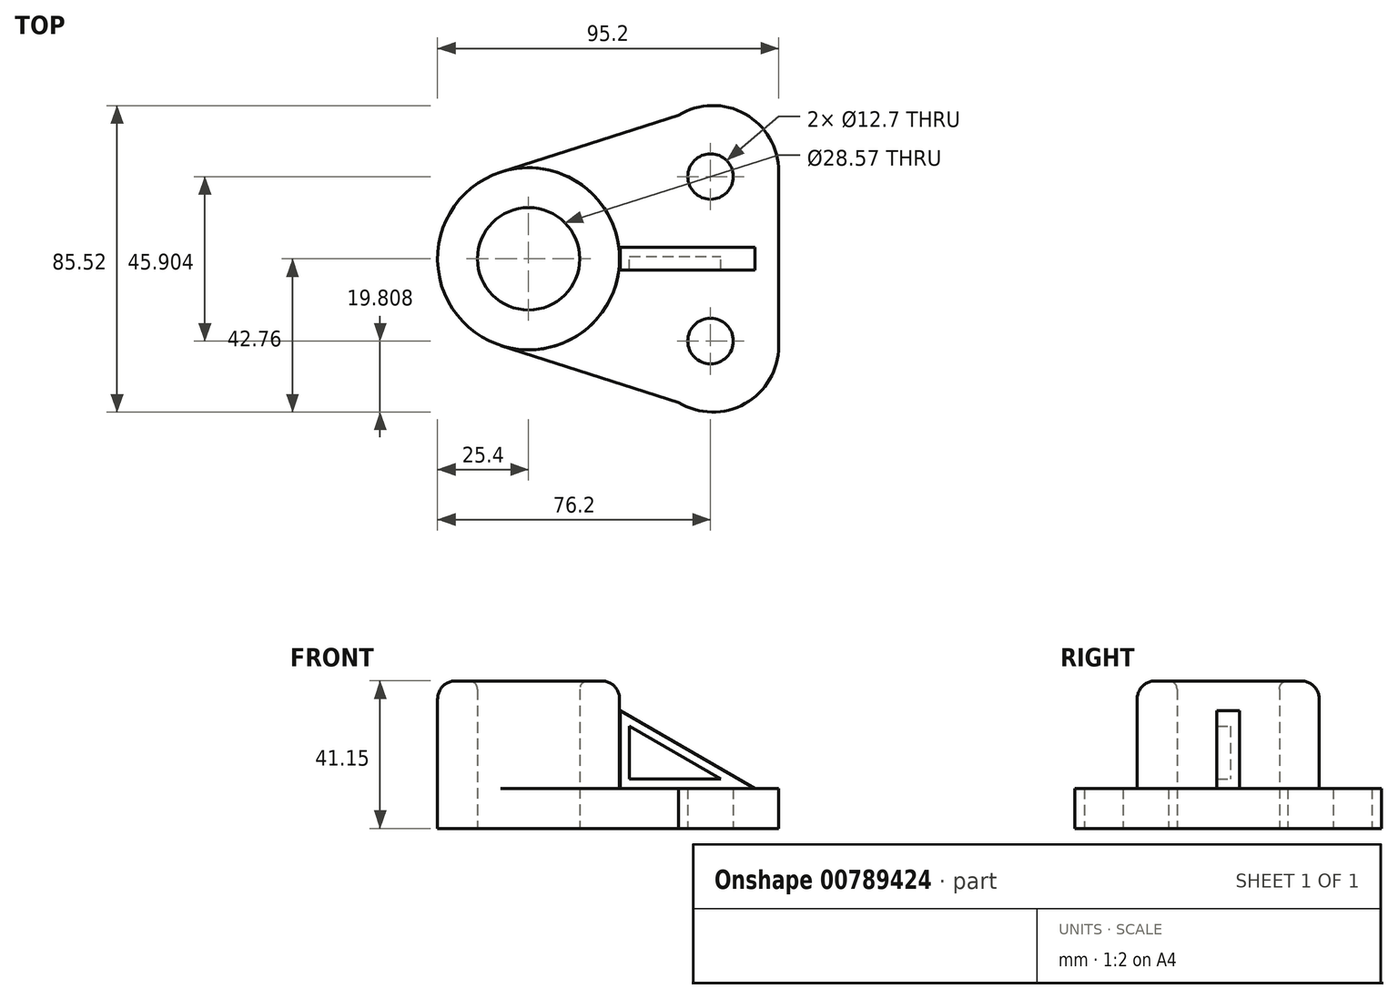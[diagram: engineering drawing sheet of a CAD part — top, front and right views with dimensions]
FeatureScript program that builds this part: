
annotation { "Feature Type Name" : "Feature", "Feature Type Description" : "" }
export const myFeature = defineFeature(function(context is Context, id is Id, definition is map)
    precondition{}
    {
        {
            var Q0;
            Q0=qCreatedBy(makeId("Top.planeOp"),FACE);
            var sketch = newSketch(context, id + "F0", { "sketchPlane" : qUnion([Q0])});
            skLineSegment(sketch, "E0", {"start": v(0, -3.9) * mm, "end": v(0, -22.95) * mm, "construction": true});
            skArc(sketch, "E1", {"start": v(19, -24.37) * mm, "mid": v(19.05, -22.95) * mm, "end": v(19, -21.54) * mm});
            skCircle(sketch, "E2", {"center": v(0, -22.95) * mm, "radius": 6.35 * mm});
            skLineSegment(sketch, "E3", {"start": v(0, -22.95) * mm, "end": v(-6.35, -22.95) * mm, "construction": true});
            skLineSegment(sketch, "E4", {"start": v(-50.8, -22.95) * mm, "end": v(-50.8, 0) * mm, "construction": true});
            skCircle(sketch, "E5", {"center": v(-50.8, 0) * mm, "radius": 25.4 * mm});
            skCircle(sketch, "E6", {"center": v(-50.8, 0) * mm, "radius": 14.29 * mm});
            skLineSegment(sketch, "E7", {"start": v(-58.55, -24.19) * mm, "end": v(-8.94, -40.1) * mm});
            skPoint(sketch, "E8.end.orphan", {"position": v(-8.94, 51.02) * mm});
            skPoint(sketch, "E8.start.orphan", {"position": v(-58.55, 24.19) * mm});
            skPoint(sketch, "E9.orphan", {"position": v(0, 34.2) * mm});
            skLineSegment(sketch, "E10", {"start": v(19, -24.37) * mm, "end": v(19, 0) * mm});
            skLineSegment(sketch, "E11", {"start": v(19, 0) * mm, "end": v(-25.4, 0) * mm});
            skArc(sketch, "E12", {"start": v(-8.94, -40.1) * mm, "mid": v(9.62, -40.4) * mm, "end": v(19, -24.37) * mm});
            skSolve(sketch);
        }
        {
            var Q0;
            Q0=makeQuery(id+"F0.imprint","IMPRINT",FACE,{"disambiguationData":[TD([[makeQuery(id+"F0.imprint","IMPRINT",EDGE,{"derivedFrom":sQuery(id+"F0.wireOp",EDGE,"E6")}),-1.0]])]});
            extrude(context, id + "F1", {"entities" : qUnion([Q0]), "depth" : 41.15 * mm, "offsetDistance" : 25.4 * mm});
        }
        {
            var Q0;
            Q0=makeQuery(id+"F0.imprint","IMPRINT",FACE,{"disambiguationData":[TD([[makeQuery(id+"F0.imprint","IMPRINT",EDGE,{"derivedFrom":sQuery(id+"F0.wireOp",EDGE,"E2")}),-1.0]])]});
            extrude(context, id + "F2", {"entities" : qUnion([Q0]), "operationType" : NewBodyOperationType.ADD, "depth" : 11.18 * mm, "offsetDistance" : 25.4 * mm});
        }
        {
            var Q0;
            Q0=makeQuery(id+"F2.opExtrude","CAP_FACE",FACE,{"disambiguationData":[OSD([sQuery(id+"F0.wireOp",EDGE,"E2"),sQuery(id+"F0.wireOp",EDGE,"E5"),sQuery(id+"F0.wireOp",EDGE,"E7"),sQuery(id+"F0.wireOp",EDGE,"E10"),sQuery(id+"F0.wireOp",EDGE,"E11"),sQuery(id+"F0.wireOp",EDGE,"E12")])],"isStart":false});
            var sketch = newSketch(context, id + "F3", { "sketchPlane" : qUnion([Q0])});
            skPoint(sketch, "E13.0", {"position": v(-25.4, 0) * mm});
            skLineSegment(sketch, "E14.0", {"start": v(19, 0) * mm, "end": v(-25.4, 0) * mm});
            skCircle(sketch, "E15.0", {"center": v(-50.8, 0) * mm, "radius": 25.4 * mm});
            skLineSegment(sketch, "E16", {"start": v(19, 0) * mm, "end": v(15.7, 0) * mm, "construction": true});
            skLineSegment(sketch, "E17", {"start": v(15.7, 0) * mm, "end": v(-25.4, 0) * mm});
            skLineSegment(sketch, "E18", {"start": v(-25.4, 0) * mm, "end": v(15.7, 0) * mm});
            skSolve(sketch);
        }
        {
            var Q0;
            Q0=qSketchRegion(id+"F3",true);
            extrude(context, id + "F4", {"entities" : qUnion([Q0]), "operationType" : NewBodyOperationType.ADD, "depth" : 25.4 * mm, "offsetDistance" : 25.4 * mm});
        }
        {
            var sketch = newSketch(context, id + "F5", { "sketchPlane" : qUnion([])});
            skLineSegment(sketch, "E19", {"start": v(0, 41.4) * mm, "end": v(0, 11.3) * mm});
            skSolve(sketch);
        }
        {
            var Q0;
            Q0=makeQuery(id+"F3.imprint","IMPRINT",FACE,{"disambiguationData":[TD([[makeQuery(id+"F3.imprint","IMPRINT",EDGE,{"derivedFrom":sQuery(id+"F3.wireOp",EDGE,"E14.0")}),1.0]])]});
            var sketch = newSketch(context, id + "F6", { "sketchPlane" : qUnion([Q0])});
            skLineSegment(sketch, "E20", {"start": v(-25.41, 0) * mm, "end": v(15.71, 0) * mm});
            skSolve(sketch);
        }
        {
            var Q0;
            Q0=makeQuery(id+"F1.opExtrude","SWEPT_BODY",BODY,{"disambiguationData":[OSD([sQuery(id+"F0.wireOp",EDGE,"E5"),sQuery(id+"F0.wireOp",EDGE,"E6")])]});
            var Q1;
            Q1=qCreatedBy(makeId("Front.planeOp"),FACE);
            mirror(context, id + "F7", {"operationType" : NewBodyOperationType.ADD, "entities" : qUnion([Q0]), "mirrorPlane" : qUnion([Q1])});
        }
        {
            var Q0;
            Q0=makeQuery(id+"F4.opExtrude","CAP_FACE",FACE,{"disambiguationData":[OSD([sQuery(id+"F3.wireOp",EDGE,"E15.0")])],"isStart":false});
            extrude(context, id + "F8", {"entities" : qUnion([Q0]), "operationType" : NewBodyOperationType.REMOVE, "endBound" : BoundingType.THROUGH_ALL, "oppositeDirection" : true, "depth" : 25.4 * mm, "offsetDistance" : 25.4 * mm});
        }
        {
            var Q0;
            Q0=qCreatedBy(makeId("Front.planeOp"),FACE);
            var sketch = newSketch(context, id + "F9", { "sketchPlane" : qUnion([Q0])});
            skLineSegment(sketch, "E21.0", {"start": v(-25.15, 41.4) * mm, "end": v(-25.15, 11.3) * mm});
            skLineSegment(sketch, "E22.0", {"start": v(-25.41, 11.18) * mm, "end": v(15.71, 11.18) * mm});
            skLineSegment(sketch, "E23", {"start": v(-25.15, 32.86) * mm, "end": v(12.41, 11.18) * mm});
            skLineSegment(sketch, "E24", {"start": v(-25.15, 32.86) * mm, "end": v(-25.15, 11.3) * mm});
            skLineSegment(sketch, "E25", {"start": v(12.41, 11.18) * mm, "end": v(-25.15, 11.3) * mm});
            skSolve(sketch);
        }
        {
            var Q0;
            Q0=makeQuery(id+"F1.opExtrude","CAP_EDGE",EDGE,{"disambiguationData":[OSD([sQuery(id+"F0.wireOp",EDGE,"E5")])],"isStart":false});
            var Q1;
            {var subQ0=makeQuery(id+"F2.opExtrude","CAP_EDGE",EDGE,{"disambiguationData":[OSD([sQuery(id+"F0.wireOp",EDGE,"E5")])],"isStart":false});Q1=makeQuery(id+"F7.boolean.opBoolean","MERGE",EDGE,{"derivedFrom":[subQ0,makeQuery(id+"F7.opPattern","COPY",EDGE,{"derivedFrom":subQ0,"instanceName":"1"})]});}
            fillet(context, id + "F10", {"entities" : qUnion([Q0, Q1]), "radius" : 5.08 * mm, "tangentPropagation" : true, "allowEdgeOverflow" : false});
        }
        {
            var Q0;
            {var subQ0=sQuery(id+"F9.wireOp",EDGE,"E23");Q0=makeQuery(id+"F9.imprint","IMPRINT",FACE,{"disambiguationData":[TD([[makeQuery(id+"F9.imprint","IMPRINT",EDGE,{"derivedFrom":subQ0}),-1.0]])]});}
            extrude(context, id + "F11", {"entities" : qUnion([Q0]), "depth" : 3.17 * mm, "offsetDistance" : 25.4 * mm, "hasSecondDirection" : true, "secondDirectionOppositeDirection" : true, "secondDirectionDepth" : 3.17 * mm});
        }
        {
            var Q0;
            Q0=makeQuery(id+"F11.opExtrude","CAP_FACE",FACE,{"disambiguationData":[OSD([sQuery(id+"F9.wireOp",EDGE,"E21.0"),sQuery(id+"F9.wireOp",EDGE,"E23"),sQuery(id+"F9.wireOp",EDGE,"E25")])],"isStart":false});
            shell(context, id + "F12", {"entities" : qUnion([Q0]), "thickness" : 2.54 * mm});
        }
        {
            var Q0;
            Q0=makeQuery(id+"F1.opExtrude","CAP_EDGE",EDGE,{"disambiguationData":[OSD([sQuery(id+"F0.wireOp",EDGE,"E6")])],"isStart":false});
            fillet(context, id + "F13", {"entities" : qUnion([Q0]), "radius" : 2.3 * mm, "tangentPropagation" : true, "allowEdgeOverflow" : false});
        }
    });
